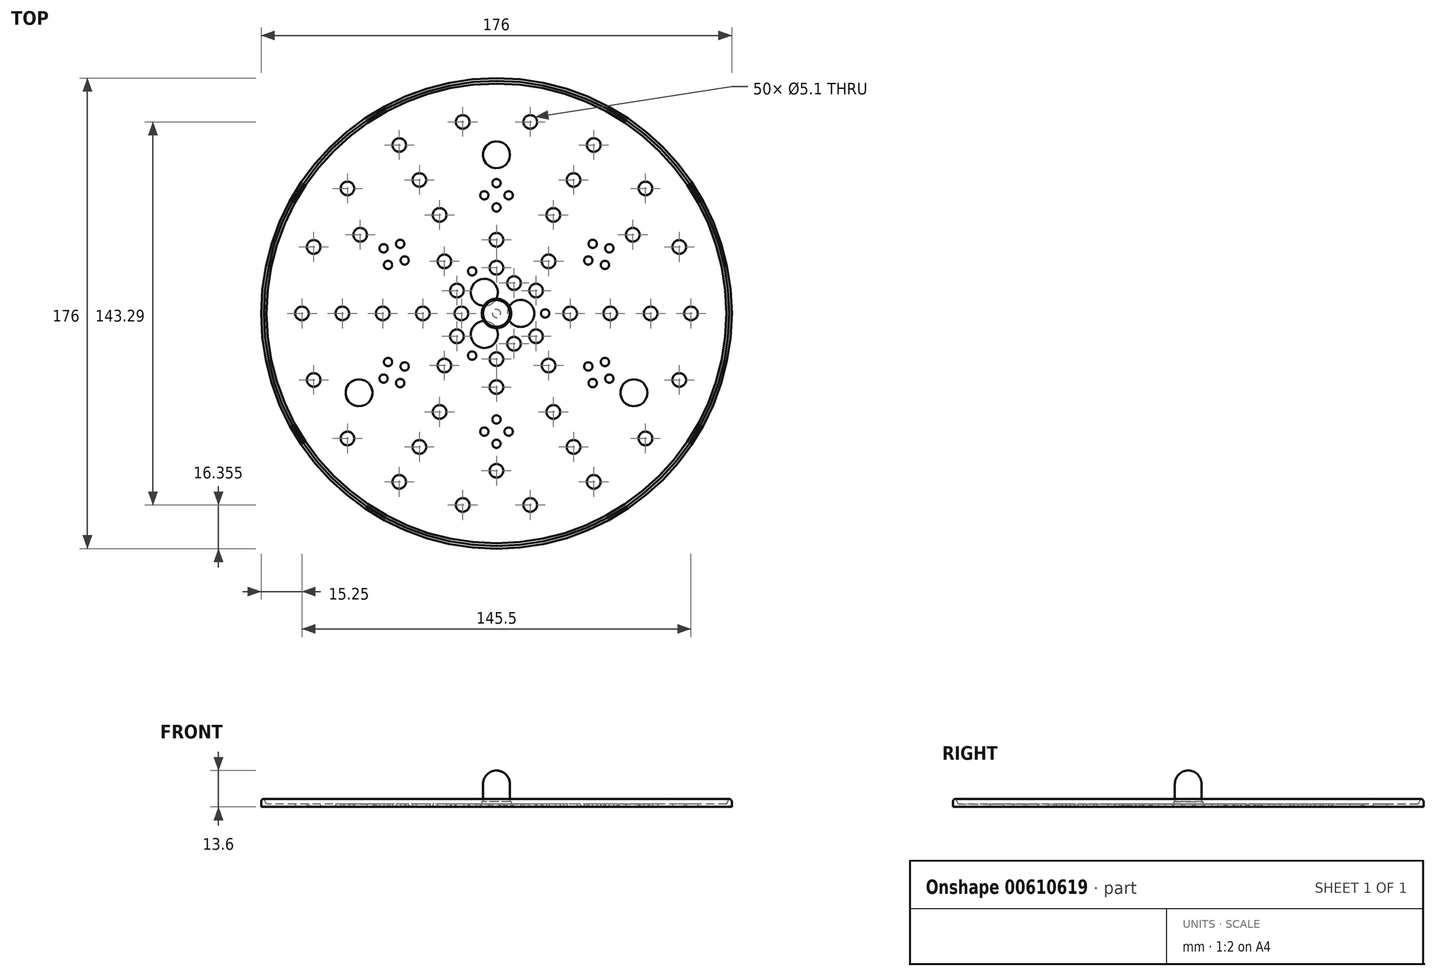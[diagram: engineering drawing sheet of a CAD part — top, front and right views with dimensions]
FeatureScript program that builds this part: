
annotation { "Feature Type Name" : "Feature", "Feature Type Description" : "" }
export const myFeature = defineFeature(function(context is Context, id is Id, definition is map)
    precondition{}
    {
        {
            var Q0;
            Q0=qCreatedBy(makeId("Top.planeOp"),FACE);
            var sketch = newSketch(context, id + "F0", { "sketchPlane" : qUnion([Q0])});
            skCircle(sketch, "E0", {"center": v(0, 0) * mm, "radius": 1.5 * mm});
            skCircle(sketch, "E1", {"center": v(0, 0) * mm, "radius": 1.87 * mm});
            skSolve(sketch);
        }
        {
            var Q0;
            Q0=makeQuery(id+"F0.imprint","IMPRINT",FACE,{"disambiguationData":[TD([[makeQuery(id+"F0.imprint","IMPRINT",EDGE,{"derivedFrom":sQuery(id+"F0.wireOp",EDGE,"E0")}),-1.0]])]});
            var Q1;
            Q1=makeQuery(id+"F0.imprint","IMPRINT",FACE,{"disambiguationData":[TD([[makeQuery(id+"F0.imprint","IMPRINT",EDGE,{"derivedFrom":sQuery(id+"F0.wireOp",EDGE,"E0")}),1.0]])]});
            extrude(context, id + "F1", {"entities" : qUnion([Q0, Q1]), "depth" : 1 * mm, "offsetDistance" : 25 * mm});
        }
        {
            var Q0;
            Q0=makeQuery(id+"F0.imprint","IMPRINT",FACE,{"disambiguationData":[TD([[makeQuery(id+"F0.imprint","IMPRINT",EDGE,{"derivedFrom":sQuery(id+"F0.wireOp",EDGE,"E0")}),1.0]])]});
            var Q1;
            Q1=sQuery(id+"F0.wireOp",EDGE,"E0");
            extrude(context, id + "F2", {"entities" : qUnion([Q0]), "operationType" : NewBodyOperationType.ADD, "surfaceEntities" : qUnion([Q1]), "depth" : 5.5 * mm, "offsetDistance" : 25 * mm});
        }
        {
            var Q0;
            Q0=makeQuery(id+"F2.opExtrude","CAP_EDGE",EDGE,{"disambiguationData":[OSD([sQuery(id+"F0.wireOp",EDGE,"E0")])],"isStart":false});
            fillet(context, id + "F3", {"entities" : qUnion([Q0]), "radius" : 1.5 * mm, "tangentPropagation" : true, "allowEdgeOverflow" : false});
        }
        {
            var Q0;
            Q0=qCreatedBy(makeId("Top.planeOp"),FACE);
            var sketch = newSketch(context, id + "F4", { "sketchPlane" : qUnion([Q0])});
            skCircle(sketch, "E2", {"center": v(0, 0) * mm, "radius": 2.5 * mm});
            skCircle(sketch, "E3", {"center": v(0, 0) * mm, "radius": 2.95 * mm});
            skSolve(sketch);
        }
        {
            var Q0;
            Q0=makeQuery(id+"F4.imprint","IMPRINT",FACE,{"disambiguationData":[TD([[makeQuery(id+"F4.imprint","IMPRINT",EDGE,{"derivedFrom":sQuery(id+"F4.wireOp",EDGE,"E2")}),1.0]])]});
            var Q1;
            Q1=makeQuery(id+"F4.imprint","IMPRINT",FACE,{"disambiguationData":[TD([[makeQuery(id+"F4.imprint","IMPRINT",EDGE,{"derivedFrom":sQuery(id+"F4.wireOp",EDGE,"E2")}),-1.0]])]});
            extrude(context, id + "F5", {"entities" : qUnion([Q0, Q1]), "depth" : 1 * mm, "offsetDistance" : 25 * mm});
        }
        {
            var Q0;
            Q0=makeQuery(id+"F4.imprint","IMPRINT",FACE,{"disambiguationData":[TD([[makeQuery(id+"F4.imprint","IMPRINT",EDGE,{"derivedFrom":sQuery(id+"F4.wireOp",EDGE,"E2")}),1.0]])]});
            extrude(context, id + "F6", {"entities" : qUnion([Q0]), "operationType" : NewBodyOperationType.ADD, "depth" : 9.7 * mm, "offsetDistance" : 25 * mm});
        }
        {
            var Q0;
            Q0=makeQuery(id+"F6.opExtrude","CAP_EDGE",EDGE,{"disambiguationData":[OSD([sQuery(id+"F4.wireOp",EDGE,"E2")])],"isStart":false});
            fillet(context, id + "F7", {"entities" : qUnion([Q0]), "radius" : 2.5 * mm, "tangentPropagation" : true, "allowEdgeOverflow" : false});
        }
        {
            var Q0;
            Q0=qCreatedBy(makeId("Top.planeOp"),FACE);
            var sketch = newSketch(context, id + "F8", { "sketchPlane" : qUnion([Q0])});
            skCircle(sketch, "E4", {"center": v(0, 0) * mm, "radius": 5 * mm});
            skCircle(sketch, "E5", {"center": v(0, 0) * mm, "radius": 5.5 * mm});
            skSolve(sketch);
        }
        {
            var Q0;
            Q0=makeQuery(id+"F8.imprint","IMPRINT",FACE,{"disambiguationData":[TD([[makeQuery(id+"F8.imprint","IMPRINT",EDGE,{"derivedFrom":sQuery(id+"F8.wireOp",EDGE,"E4")}),-1.0]])]});
            var Q1;
            Q1=makeQuery(id+"F8.imprint","IMPRINT",FACE,{"disambiguationData":[TD([[makeQuery(id+"F8.imprint","IMPRINT",EDGE,{"derivedFrom":sQuery(id+"F8.wireOp",EDGE,"E4")}),1.0]])]});
            extrude(context, id + "F9", {"entities" : qUnion([Q0, Q1]), "depth" : 2 * mm, "offsetDistance" : 25 * mm});
        }
        {
            var Q0;
            Q0=makeQuery(id+"F8.imprint","IMPRINT",FACE,{"disambiguationData":[TD([[makeQuery(id+"F8.imprint","IMPRINT",EDGE,{"derivedFrom":sQuery(id+"F8.wireOp",EDGE,"E4")}),1.0]])]});
            extrude(context, id + "F10", {"entities" : qUnion([Q0]), "operationType" : NewBodyOperationType.ADD, "depth" : 13.6 * mm, "offsetDistance" : 25 * mm});
        }
        {
            var Q0;
            Q0=makeQuery(id+"F10.opExtrude","CAP_EDGE",EDGE,{"disambiguationData":[OSD([sQuery(id+"F8.wireOp",EDGE,"E4")])],"isStart":false});
            fillet(context, id + "F11", {"entities" : qUnion([Q0]), "radius" : 5 * mm, "tangentPropagation" : true, "allowEdgeOverflow" : false});
        }
        {
            var Q0;
            Q0=qCreatedBy(makeId("Top.planeOp"),FACE);
            var sketch = newSketch(context, id + "F12", { "sketchPlane" : qUnion([Q0])});
            skPoint(sketch, "E6", {"position": v(9.1, 0) * mm});
            skCircle(sketch, "E7", {"center": v(9.1, 0) * mm, "radius": 5.05 * mm});
            skCircle(sketch, "E8", {"center": v(0, 0) * mm, "radius": 1.55 * mm});
            skCircle(sketch, "E9.1.0", {"center": v(-4.55, 7.88) * mm, "radius": 5.05 * mm});
            skCircle(sketch, "E9.2.0", {"center": v(-4.55, -7.88) * mm, "radius": 5.05 * mm});
            skCircle(sketch, "E10", {"center": v(-13.1, 0) * mm, "radius": 2.55 * mm});
            skCircle(sketch, "E11.1.0", {"center": v(6.55, -11.34) * mm, "radius": 2.55 * mm});
            skCircle(sketch, "E11.2.0", {"center": v(6.55, 11.34) * mm, "radius": 2.55 * mm});
            skCircle(sketch, "E12", {"center": v(0, -17.1) * mm, "radius": 2.55 * mm});
            skCircle(sketch, "E13.1.0", {"center": v(14.8, -8.55) * mm, "radius": 2.55 * mm});
            skCircle(sketch, "E13.2.0", {"center": v(14.8, 8.55) * mm, "radius": 2.55 * mm});
            skCircle(sketch, "E13.3.0", {"center": v(0, 17.1) * mm, "radius": 2.55 * mm});
            skCircle(sketch, "E13.4.0", {"center": v(-14.8, 8.55) * mm, "radius": 2.55 * mm});
            skCircle(sketch, "E13.5.0", {"center": v(-14.8, -8.55) * mm, "radius": 2.55 * mm});
            skCircle(sketch, "E14", {"center": v(0, 0) * mm, "radius": 88 * mm});
            skCircle(sketch, "E15", {"center": v(18.2, 0) * mm, "radius": 1.55 * mm});
            skCircle(sketch, "E16.1.0", {"center": v(-9.1, 15.76) * mm, "radius": 1.55 * mm});
            skCircle(sketch, "E16.2.0", {"center": v(-9.1, -15.76) * mm, "radius": 1.55 * mm});
            skCircle(sketch, "E17", {"center": v(27.55, 0) * mm, "radius": 2.55 * mm});
            skCircle(sketch, "E18.1.0", {"center": v(19.48, 19.48) * mm, "radius": 2.55 * mm});
            skCircle(sketch, "E18.2.0", {"center": v(0, 27.55) * mm, "radius": 2.55 * mm});
            skCircle(sketch, "E18.3.0", {"center": v(-19.48, 19.48) * mm, "radius": 2.55 * mm});
            skCircle(sketch, "E18.4.0", {"center": v(-27.55, 0) * mm, "radius": 2.55 * mm});
            skCircle(sketch, "E18.5.0", {"center": v(-19.48, -19.48) * mm, "radius": 2.55 * mm});
            skCircle(sketch, "E18.6.0", {"center": v(0, -27.55) * mm, "radius": 2.55 * mm});
            skCircle(sketch, "E18.7.0", {"center": v(19.48, -19.48) * mm, "radius": 2.55 * mm});
            skCircle(sketch, "E19", {"center": v(42.55, 0) * mm, "radius": 2.55 * mm});
            skCircle(sketch, "E20", {"center": v(57.65, 0) * mm, "radius": 2.55 * mm});
            skCircle(sketch, "E21.1.0", {"center": v(28.83, 49.93) * mm, "radius": 2.55 * mm});
            skCircle(sketch, "E21.1.1", {"center": v(21.28, 36.85) * mm, "radius": 2.55 * mm});
            skCircle(sketch, "E21.2.0", {"center": v(-28.82, 49.93) * mm, "radius": 2.55 * mm});
            skCircle(sketch, "E21.2.1", {"center": v(-21.27, 36.85) * mm, "radius": 2.55 * mm});
            skCircle(sketch, "E21.3.0", {"center": v(-57.65, 0) * mm, "radius": 2.55 * mm});
            skCircle(sketch, "E21.3.1", {"center": v(-42.55, 0) * mm, "radius": 2.55 * mm});
            skCircle(sketch, "E21.4.0", {"center": v(-28.83, -49.93) * mm, "radius": 2.55 * mm});
            skCircle(sketch, "E21.4.1", {"center": v(-21.28, -36.85) * mm, "radius": 2.55 * mm});
            skCircle(sketch, "E21.5.0", {"center": v(28.83, -49.93) * mm, "radius": 2.55 * mm});
            skCircle(sketch, "E21.5.1", {"center": v(21.28, -36.85) * mm, "radius": 2.55 * mm});
            skCircle(sketch, "E22", {"center": v(0, -39.65) * mm, "radius": 1.55 * mm});
            skCircle(sketch, "E23", {"center": v(0, -48.75) * mm, "radius": 1.55 * mm});
            skCircle(sketch, "E24", {"center": v(-4.55, -44.2) * mm, "radius": 1.55 * mm});
            skPoint(sketch, "E25", {"position": v(0, -44.2) * mm});
            skCircle(sketch, "E26", {"center": v(4.55, -44.2) * mm, "radius": 1.55 * mm});
            skCircle(sketch, "E27.1.0", {"center": v(34.34, -19.83) * mm, "radius": 1.55 * mm});
            skCircle(sketch, "E27.1.1", {"center": v(40.55, -18.16) * mm, "radius": 1.55 * mm});
            skCircle(sketch, "E27.1.2", {"center": v(42.22, -24.38) * mm, "radius": 1.55 * mm});
            skCircle(sketch, "E27.1.3", {"center": v(36, -26.04) * mm, "radius": 1.55 * mm});
            skCircle(sketch, "E27.2.0", {"center": v(34.34, 19.82) * mm, "radius": 1.55 * mm});
            skCircle(sketch, "E27.2.1", {"center": v(36, 26.04) * mm, "radius": 1.55 * mm});
            skCircle(sketch, "E27.2.2", {"center": v(42.22, 24.37) * mm, "radius": 1.55 * mm});
            skCircle(sketch, "E27.2.3", {"center": v(40.55, 18.16) * mm, "radius": 1.55 * mm});
            skCircle(sketch, "E27.3.0", {"center": v(0, 39.65) * mm, "radius": 1.55 * mm});
            skCircle(sketch, "E27.3.1", {"center": v(-4.55, 44.2) * mm, "radius": 1.55 * mm});
            skCircle(sketch, "E27.3.2", {"center": v(0, 48.75) * mm, "radius": 1.55 * mm});
            skCircle(sketch, "E27.3.3", {"center": v(4.55, 44.2) * mm, "radius": 1.55 * mm});
            skCircle(sketch, "E27.4.0", {"center": v(-34.34, 19.83) * mm, "radius": 1.55 * mm});
            skCircle(sketch, "E27.4.1", {"center": v(-40.55, 18.16) * mm, "radius": 1.55 * mm});
            skCircle(sketch, "E27.4.2", {"center": v(-42.22, 24.38) * mm, "radius": 1.55 * mm});
            skCircle(sketch, "E27.4.3", {"center": v(-36, 26.04) * mm, "radius": 1.55 * mm});
            skCircle(sketch, "E27.5.0", {"center": v(-34.34, -19.83) * mm, "radius": 1.55 * mm});
            skCircle(sketch, "E27.5.1", {"center": v(-36, -26.04) * mm, "radius": 1.55 * mm});
            skCircle(sketch, "E27.5.2", {"center": v(-42.22, -24.38) * mm, "radius": 1.55 * mm});
            skCircle(sketch, "E27.5.3", {"center": v(-40.55, -18.16) * mm, "radius": 1.55 * mm});
            skCircle(sketch, "E28", {"center": v(0, 59.35) * mm, "radius": 5.05 * mm});
            skCircle(sketch, "E29.1.0", {"center": v(-51.4, -29.67) * mm, "radius": 5.05 * mm});
            skCircle(sketch, "E29.2.0", {"center": v(51.4, -29.68) * mm, "radius": 5.05 * mm});
            skCircle(sketch, "E30", {"center": v(-72.75, 0) * mm, "radius": 2.55 * mm});
            skCircle(sketch, "E31.1.0", {"center": v(-68.36, -24.88) * mm, "radius": 2.55 * mm});
            skCircle(sketch, "E31.2.0", {"center": v(-55.73, -46.76) * mm, "radius": 2.55 * mm});
            skCircle(sketch, "E31.3.0", {"center": v(-36.38, -63) * mm, "radius": 2.55 * mm});
            skCircle(sketch, "E31.4.0", {"center": v(-12.63, -71.64) * mm, "radius": 2.55 * mm});
            skCircle(sketch, "E31.5.0", {"center": v(12.63, -71.64) * mm, "radius": 2.55 * mm});
            skCircle(sketch, "E31.6.0", {"center": v(36.37, -63) * mm, "radius": 2.55 * mm});
            skCircle(sketch, "E31.7.0", {"center": v(55.73, -46.76) * mm, "radius": 2.55 * mm});
            skCircle(sketch, "E31.8.0", {"center": v(68.36, -24.88) * mm, "radius": 2.55 * mm});
            skCircle(sketch, "E31.9.0", {"center": v(72.75, 0) * mm, "radius": 2.55 * mm});
            skCircle(sketch, "E31.10.0", {"center": v(68.36, 24.88) * mm, "radius": 2.55 * mm});
            skCircle(sketch, "E31.11.0", {"center": v(55.73, 46.76) * mm, "radius": 2.55 * mm});
            skCircle(sketch, "E31.12.0", {"center": v(36.38, 63) * mm, "radius": 2.55 * mm});
            skCircle(sketch, "E31.13.0", {"center": v(12.63, 71.64) * mm, "radius": 2.55 * mm});
            skCircle(sketch, "E31.14.0", {"center": v(-12.63, 71.64) * mm, "radius": 2.55 * mm});
            skCircle(sketch, "E31.15.0", {"center": v(-36.37, 63) * mm, "radius": 2.55 * mm});
            skCircle(sketch, "E31.16.0", {"center": v(-55.73, 46.76) * mm, "radius": 2.55 * mm});
            skCircle(sketch, "E31.17.0", {"center": v(-68.36, 24.88) * mm, "radius": 2.55 * mm});
            skCircle(sketch, "E32", {"center": v(0, -58.85) * mm, "radius": 2.55 * mm});
            skCircle(sketch, "E33.1.0", {"center": v(50.97, 29.42) * mm, "radius": 2.55 * mm});
            skCircle(sketch, "E33.2.0", {"center": v(-50.97, 29.43) * mm, "radius": 2.55 * mm});
            skCircle(sketch, "E34", {"center": v(0, 0) * mm, "radius": 86 * mm});
            skSolve(sketch);
        }
        {
            var Q0;
            Q0=makeQuery(id+"F12.imprint","IMPRINT",FACE,{"disambiguationData":[TD([[makeQuery(id+"F12.imprint","IMPRINT",EDGE,{"derivedFrom":sQuery(id+"F12.wireOp",EDGE,"E7")}),-1.0]])]});
            var Q1;
            Q1=makeQuery(id+"F12.imprint","IMPRINT",FACE,{"disambiguationData":[TD([[makeQuery(id+"F12.imprint","IMPRINT",EDGE,{"derivedFrom":sQuery(id+"F12.wireOp",EDGE,"E14")}),1.0]])]});
            extrude(context, id + "F13", {"entities" : qUnion([Q0, Q1]), "depth" : 1 * mm, "offsetDistance" : 25 * mm});
        }
        {
            var Q0;
            Q0=makeQuery(id+"F12.imprint","IMPRINT",FACE,{"disambiguationData":[TD([[makeQuery(id+"F12.imprint","IMPRINT",EDGE,{"derivedFrom":sQuery(id+"F12.wireOp",EDGE,"E14")}),1.0]])]});
            extrude(context, id + "F14", {"entities" : qUnion([Q0]), "operationType" : NewBodyOperationType.ADD, "depth" : 3 * mm, "offsetDistance" : 25 * mm});
        }
        {
            var Q0;
            Q0=makeQuery(id+"F14.opExtrude","CAP_EDGE",EDGE,{"disambiguationData":[OSD([sQuery(id+"F12.wireOp",EDGE,"E14")])],"isStart":false});
            fillet(context, id + "F15", {"entities" : qUnion([Q0]), "radius" : 1 * mm, "tangentPropagation" : true, "allowEdgeOverflow" : false});
        }
        {
            var Q0;
            Q0=makeQuery(id+"F14.opExtrude","CAP_EDGE",EDGE,{"disambiguationData":[OSD([sQuery(id+"F12.wireOp",EDGE,"E34")])],"isStart":false});
            chamfer(context, id + "F16", {"entities" : qUnion([Q0]), "chamferType" : ChamferType.TWO_OFFSETS, "width1" : 2 * mm, "oppositeDirection" : false, "width2" : 1 * mm, "tangentPropagation" : true});
        }
        {
            var Q0;
            Q0=makeQuery(id+"F13.opExtrude","CAP_EDGE",EDGE,{"disambiguationData":[OSD([sQuery(id+"F12.wireOp",EDGE,"E9.1.0")])],"isStart":false});
            var Q1;
            Q1=makeQuery(id+"F13.opExtrude","CAP_EDGE",EDGE,{"disambiguationData":[OSD([sQuery(id+"F12.wireOp",EDGE,"E7")])],"isStart":false});
            var Q2;
            Q2=makeQuery(id+"F13.opExtrude","CAP_EDGE",EDGE,{"disambiguationData":[OSD([sQuery(id+"F12.wireOp",EDGE,"E9.2.0")])],"isStart":false});
            var Q3;
            Q3=makeQuery(id+"F13.opExtrude","CAP_EDGE",EDGE,{"disambiguationData":[OSD([sQuery(id+"F12.wireOp",EDGE,"E29.1.0")])],"isStart":false});
            var Q4;
            Q4=makeQuery(id+"F13.opExtrude","CAP_EDGE",EDGE,{"disambiguationData":[OSD([sQuery(id+"F12.wireOp",EDGE,"E29.2.0")])],"isStart":false});
            var Q5;
            Q5=makeQuery(id+"F13.opExtrude","CAP_EDGE",EDGE,{"disambiguationData":[OSD([sQuery(id+"F12.wireOp",EDGE,"E28")])],"isStart":false});
            fillet(context, id + "F17", {"entities" : qUnion([Q0, Q1, Q2, Q3, Q4, Q5]), "radius" : 1 * mm, "tangentPropagation" : true, "rho" : 0.1, "crossSection" : FilletCrossSection.CONIC, "allowEdgeOverflow" : false});
        }
    });
